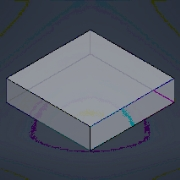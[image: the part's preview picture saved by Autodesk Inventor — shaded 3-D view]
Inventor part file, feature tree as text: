
AUTODESK INVENTOR PART (.ipt)
format: ipt  version: 2024.3 (Build 283343000, 343)  size: 135,168 bytes
history: native  units: mm
features: extrude x1, sketch x1
ambient origin geometry x8: Origin, YZ Plane, XZ Plane, XY Plane, X Axis, Y Axis, Z Axis, Center Point
bodies: Solid1 (feature_tree)
feature tree (2):
  extrude  "Extrusion1"  Depth=80.0mm
  sketch  "Sketch1"  dims[d0=80.0mm d1=80.0mm d2=30.0mm d3=0.0mm]
